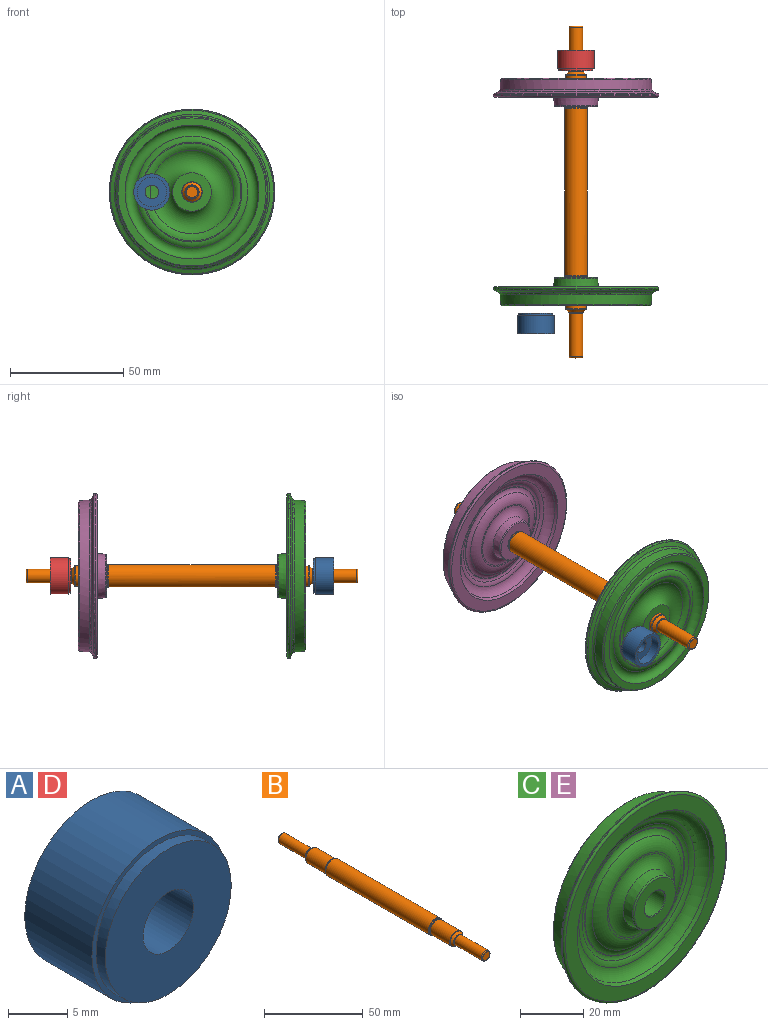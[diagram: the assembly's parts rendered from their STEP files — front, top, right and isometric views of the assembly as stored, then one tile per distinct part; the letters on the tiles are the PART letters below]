
ASSEMBLY  parts=5 mates=4
PART A: 8 faces, bbox 16x9.1x16 mm
  f0: plane 13x13mm, normal (0,1,0), area 104.5mm2, adj f3,f4
  f1: cylinder r=7.5mm len=15mm, axis (0,1,0), area 51.8mm2, adj f2,f7
  f2: plane 15x15mm, normal (0,-1,0), area 148.4mm2, adj f1,f3
  f3: cylinder r=3mm len=6mm, axis (0,-1,0), area 94.2mm2, adj f0,f2
  f4: cylinder r=6.5mm len=13mm, axis (0,-1,0), area 167.4mm2, adj f0,f6
  f5: cylinder r=8mm len=16mm, axis (0,-1,0), area 402.1mm2, adj f6,f7
  f6: plane 16x16mm, normal (0,1,0), area 68.3mm2, adj f4,f5
  f7: plane 16x16mm, normal (0,-1,0), area 24.3mm2, adj f1,f5
PART B: 21 faces, bbox 10.8x146.5x10.8 mm
  f0: cylinder r=5mm len=73.51mm, axis (0,1,0), area 2309.4mm2, adj f14,f15
  f1: cylinder r=4.5mm len=13.8mm, axis (0,1,0), area 390.2mm2, adj f12,f20
  f2: cylinder r=3mm len=19.29mm, axis (0,1,0), area 363.7mm2, adj f18,f19
  f3: plane 5x5mm, normal (0,-1,0), area 19.6mm2, adj f19
  f4: cylinder r=4.5mm len=13.81mm, axis (0,-1,0), area 390.3mm2, adj f11,f13
  f5: cylinder r=3mm len=19.29mm, axis (0,-1,0), area 363.7mm2, adj f16,f17
  f6: plane 5x5mm, normal (0,1,0), area 19.6mm2, adj f17
  f7: cone r=4.5mm half-angle=40deg, axis (0,1,0), area 12.4mm2, adj f15,f20
  f8: cone r=5mm half-angle=40deg, axis (0,-1,0), area 12.4mm2, adj f13,f14
  f9: cone r=3mm half-angle=45deg, axis (0,1,0), area 40.2mm2, adj f12,f18
  f10: cone r=3mm half-angle=45deg, axis (0,-1,0), area 40.2mm2, adj f11,f16
  f11: torus R=4mm, axis (0,1,0), area 11mm2, adj f4,f10
  f12: torus R=4mm, axis (0,-1,0), area 11mm2, adj f1,f9
  f13: torus R=5mm, axis (0,1,0), area 10mm2, adj f4,f8
  f14: torus R=4.5mm, axis (0,1,0), area 10.9mm2, adj f0,f8
  f15: torus R=4.5mm, axis (0,-1,0), area 10.9mm2, adj f0,f7
  f16: torus R=3.5mm, axis (0,1,0), area 7.5mm2, adj f5,f10
  f17: torus R=2.5mm, axis (0,1,0), area 13.9mm2, adj f5,f6
  f18: torus R=3.5mm, axis (0,-1,0), area 7.5mm2, adj f2,f9
  f19: torus R=2.5mm, axis (0,-1,0), area 13.9mm2, adj f2,f3
  f20: torus R=5mm, axis (0,-1,0), area 10mm2, adj f1,f7
PART C: 29 faces, bbox 79x15.2x79 mm
  f0: torus R=26.65mm, axis (0,1,0), area 1163.7mm2, adj f1,f25
  f1: plane 65.39x65.39mm, normal (0,1,0), area 620.6mm2, adj f0,f12
  f2: plane 17.01x17.01mm, normal (0,1,0), area 163.6mm2, adj f4,f23
  f3: plane 30.14x30.14mm, normal (0,-1,0), area 57.9mm2, adj f15,f20
  f4: cylinder r=4.5mm len=12.15mm, axis (0,-1,0), area 343.4mm2, adj f2,f26
  f5: cone r=36.5mm half-angle=68deg, axis (0,-1,0), area 422.8mm2, adj f9,f10
  f6: plane 71.48x71.48mm, normal (0,-1,0), area 1089.8mm2, adj f8,f16
  f7: cylinder r=36.5mm len=73mm, axis (0,1,0), area 40.4mm2, adj f8,f9
  f8: torus R=35.74mm, axis (0,-1,0), area 272.4mm2, adj f6,f7
  f9: torus R=35.74mm, axis (0,-1,0), area 206.5mm2, adj f5,f7
  f10: torus R=34.78mm, axis (0,1,0), area 288.1mm2, adj f5,f11
  f11: cone r=33.2mm half-angle=3.5deg, axis (0,-1,0), area 933.2mm2, adj f10,f12
  f12: cone r=33.23mm half-angle=46.7deg, axis (0,-1,0), area 153.2mm2, adj f1,f11
  f13: plane 18.11x18.11mm, normal (0,-1,0), area 186.8mm2, adj f26,f27
  f14: cone r=9.5mm half-angle=6.6deg, axis (0,1,0), area 227.1mm2, adj f15,f27
  f15: torus R=14.45mm, axis (0,-1,0), area 382.7mm2, adj f3,f14
  f16: cone r=30.5mm half-angle=26.6deg, axis (0,-1,0), area 262.2mm2, adj f6,f18
  f17: plane 44.53x44.53mm, normal (0,-1,0), area 36.7mm2, adj f19,f21
  f18: torus R=25.41mm, axis (0,-1,0), area 907.8mm2, adj f16,f22
  f19: torus R=22mm, axis (0,-1,0), area 321.1mm2, adj f17,f20
  f20: torus R=15.07mm, axis (0,1,0), area 586.9mm2, adj f3,f19
  f21: torus R=22.26mm, axis (0,1,0), area 222.7mm2, adj f17,f22
  f22: torus R=26.19mm, axis (0,1,0), area 338.2mm2, adj f18,f21
  f23: torus R=14.25mm, axis (0,1,0), area 960.3mm2, adj f2,f28
  f24: plane 44.12x44.12mm, normal (0,1,0), area 59mm2, adj f25,f28
  f25: torus R=22.06mm, axis (0,-1,0), area 421.2mm2, adj f0,f24
  f26: cone r=4.5mm half-angle=45deg, axis (0,-1,0), area 10.3mm2, adj f4,f13
  f27: torus R=9.06mm, axis (0,-1,0), area 42.8mm2, adj f13,f14
  f28: torus R=21.63mm, axis (0,1,0), area 441.5mm2, adj f23,f24
PART D: same geometry as A
PART E: same geometry as C
PLACE A rot(axis=(0,0,-1),180deg) t=(-53.1,-106.25,-36.33)mm
PLACE B t=(-35.41,-47.82,-36.33)mm
PLACE C rot(axis=(1,0,0),180deg) t=(-35.41,-98.03,-36.33)mm
PLACE D t=(-35.41,10.62,-36.33)mm
PLACE E t=(-35.41,2.39,-36.33)mm
MATE pin_slot D.f3 <-> B.f2  axis (0,-1,0) through (-35.41,5.62,-36.33)mm
MATE pin_slot A.f3 <-> B.f2  axis (0,1,0) through (-53.1,-101.25,-36.33)mm
MATE pin_slot E.f14 <-> B.f1  axis (0,-1,0) through (-35.41,-10.1,-36.33)mm
MATE pin_slot C.f4 <-> B.f1  axis (0,1,0) through (-35.41,-85.53,-36.33)mm
